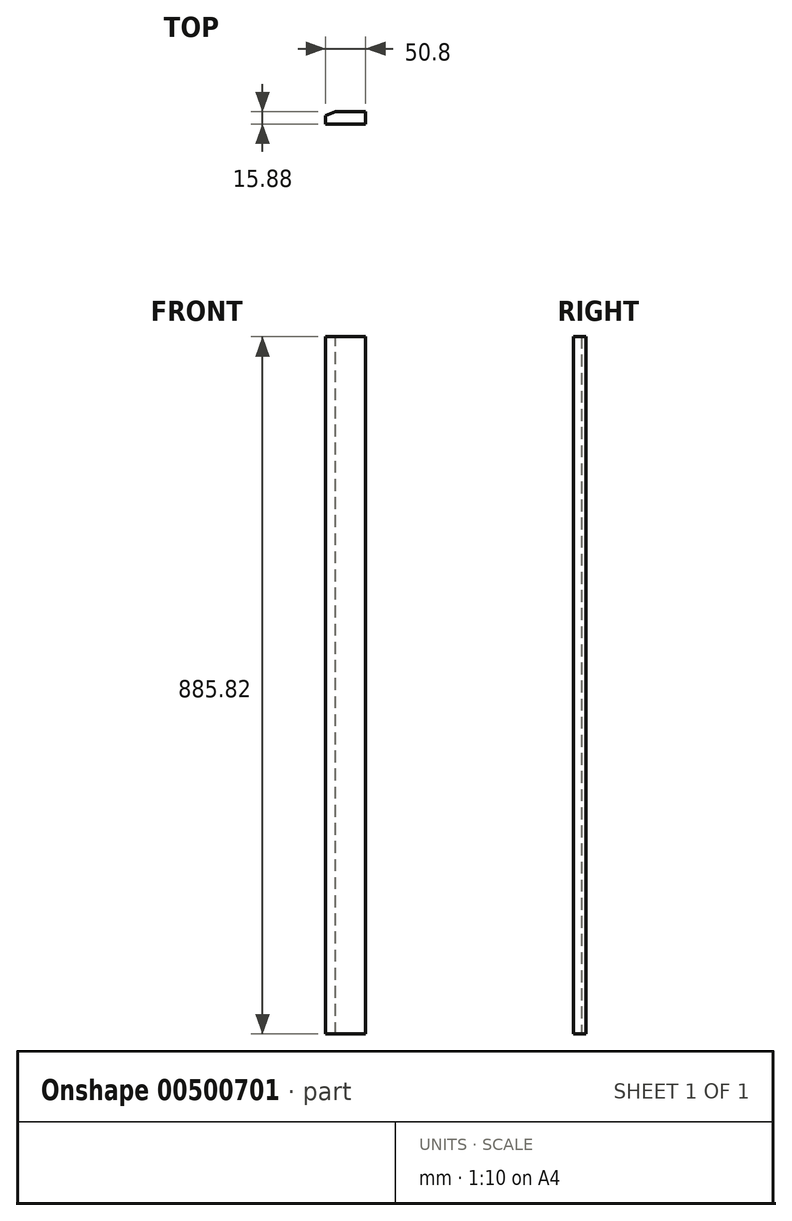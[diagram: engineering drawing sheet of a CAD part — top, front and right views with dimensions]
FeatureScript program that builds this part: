
annotation { "Feature Type Name" : "Feature", "Feature Type Description" : "" }
export const myFeature = defineFeature(function(context is Context, id is Id, definition is map)
    precondition{}
    {
        {
            var Q0;
            Q0=qCreatedBy(makeId("Front.planeOp"),FACE);
            var sketch = newSketch(context, id + "F0", { "sketchPlane" : qUnion([Q0])});
            skLineSegment(sketch, "E0.bottom", {"start": v(0, 0) * mm, "end": v(50.8, 0) * mm});
            skLineSegment(sketch, "E0.top", {"start": v(0, 885.83) * mm, "end": v(50.8, 885.83) * mm});
            skLineSegment(sketch, "E0.left", {"start": v(0, 0) * mm, "end": v(0, 885.83) * mm});
            skLineSegment(sketch, "E0.right", {"start": v(50.8, 0) * mm, "end": v(50.8, 885.83) * mm});
            skSolve(sketch);
        }
        {
            var Q0;
            Q0=makeQuery(id+"F0.imprint","IMPRINT",FACE,{"disambiguationData":[TD([[makeQuery(id+"F0.imprint","IMPRINT",EDGE,{"derivedFrom":sQuery(id+"F0.wireOp",EDGE,"E0.bottom")}),1.0]])]});
            extrude(context, id + "F1", {"entities" : qUnion([Q0]), "oppositeDirection" : true, "offsetDistance" : 25.4 * mm, "depth" : 15.88 * mm});
        }
        {
            var Q0;
            Q0=makeQuery(id+"F1.opExtrude","CAP_EDGE",EDGE,{"disambiguationData":[OSD([sQuery(id+"F0.wireOp",EDGE,"E0.left")])],"isStart":false});
            chamfer(context, id + "F2", {"entities" : qUnion([Q0]), "chamferType" : ChamferType.OFFSET_ANGLE, "width" : 12.7 * mm, "oppositeDirection" : false, "angle" : 22.5 * degree, "tangentPropagation" : true});
        }
    });
